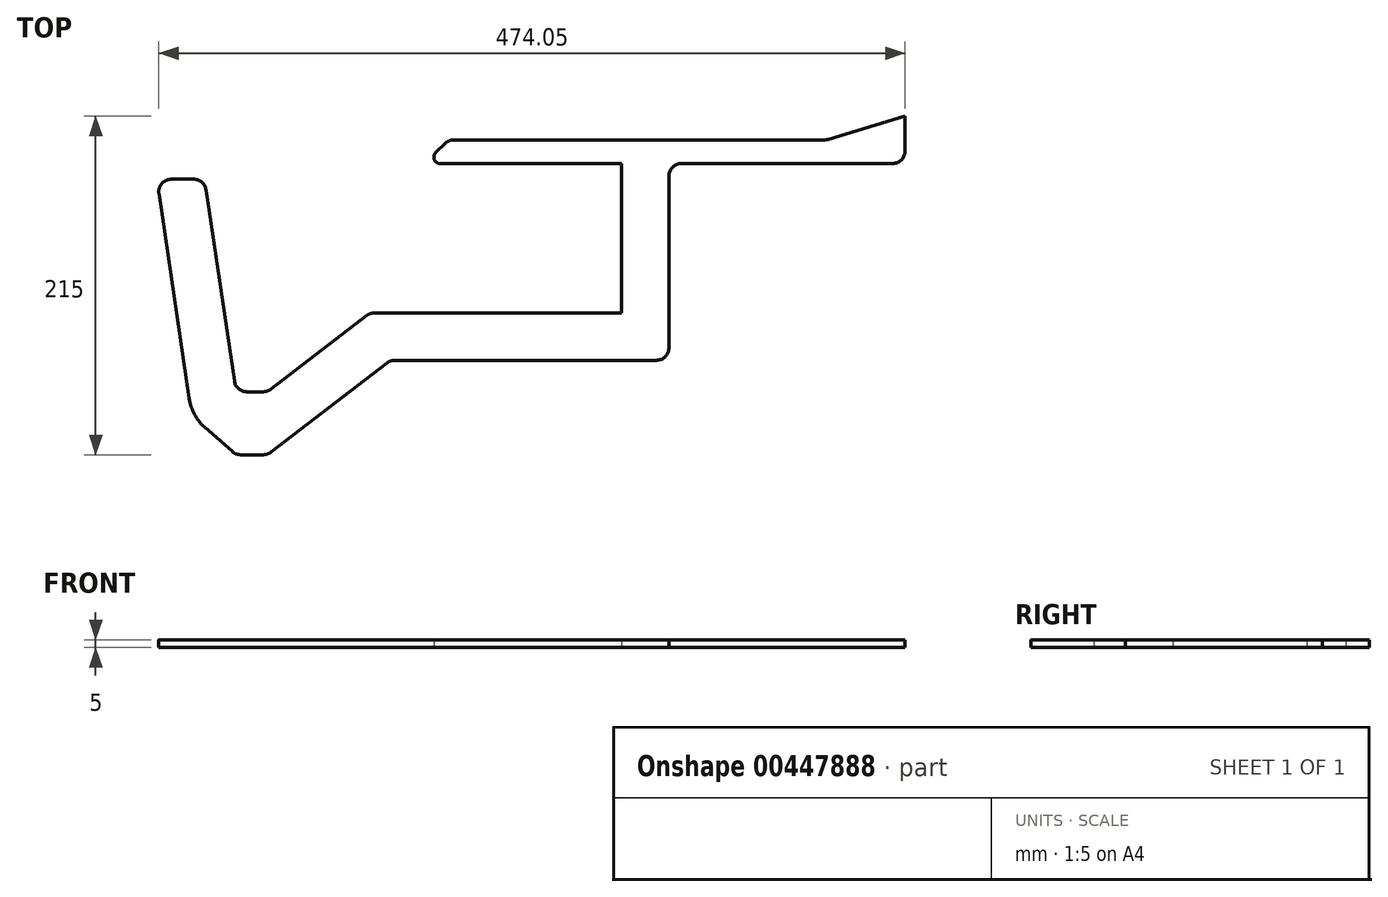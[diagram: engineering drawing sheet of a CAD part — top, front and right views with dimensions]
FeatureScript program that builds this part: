
annotation { "Feature Type Name" : "Feature", "Feature Type Description" : "" }
export const myFeature = defineFeature(function(context is Context, id is Id, definition is map)
    precondition{}
    {
        {
            var Q0;
            Q0=qCreatedBy(makeId("Top.planeOp"),FACE);
            var sketch = newSketch(context, id + "F0", { "sketchPlane" : qUnion([Q0])});
            skPoint(sketch, "E0", {"position": v(-85, 0) * mm});
            skPoint(sketch, "E1", {"position": v(-65, -135) * mm});
            skLineSegment(sketch, "E2", {"start": v(-83.99, -6.83) * mm, "end": v(-66.01, -128.17) * mm});
            skPoint(sketch, "E3", {"position": v(-45, -135) * mm});
            skPoint(sketch, "E4", {"position": v(20, -85) * mm});
            skLineSegment(sketch, "E5", {"start": v(-58.1, -135) * mm, "end": v(-47.72, -135) * mm});
            skLineSegment(sketch, "E6", {"start": v(17.84, -86.66) * mm, "end": v(-42.84, -133.34) * mm});
            skPoint(sketch, "E7", {"position": v(180, -85) * mm});
            skLineSegment(sketch, "E8", {"start": v(22.72, -85) * mm, "end": v(180, -85) * mm});
            skPoint(sketch, "E9", {"position": v(180, 10) * mm});
            skPoint(sketch, "E10", {"position": v(55, 10) * mm});
            skLineSegment(sketch, "E11", {"start": v(64.66, 10) * mm, "end": v(180, 10) * mm});
            skLineSegment(sketch, "E12", {"start": v(180, 10) * mm, "end": v(180, -85) * mm});
            skPoint(sketch, "E13", {"position": v(70, 25) * mm});
            skLineSegment(sketch, "E14", {"start": v(61.83, 16.83) * mm, "end": v(67.66, 22.66) * mm});
            skLineSegment(sketch, "E15", {"start": v(360, 18) * mm, "end": v(360, 40) * mm});
            skLineSegment(sketch, "E16", {"start": v(360, 40) * mm, "end": v(311.12, 25.34) * mm});
            skLineSegment(sketch, "E17", {"start": v(308.83, 25) * mm, "end": v(73.31, 25) * mm});
            skLineSegment(sketch, "E18", {"start": v(352, 10) * mm, "end": v(218, 10) * mm});
            skLineSegment(sketch, "E19", {"start": v(210, 2) * mm, "end": v(210, -107) * mm});
            skPoint(sketch, "E20", {"position": v(-45, -175) * mm});
            skPoint(sketch, "E21", {"position": v(-65, -175) * mm});
            skLineSegment(sketch, "E22", {"start": v(202, -115) * mm, "end": v(35.72, -115) * mm});
            skLineSegment(sketch, "E23", {"start": v(30.84, -116.66) * mm, "end": v(-42.84, -173.34) * mm});
            skLineSegment(sketch, "E24", {"start": v(-61.98, -175) * mm, "end": v(-47.72, -175) * mm});
            skLineSegment(sketch, "E25", {"start": v(-65, -135) * mm, "end": v(-94.68, -139.4) * mm});
            skLineSegment(sketch, "E26", {"start": v(-67.27, -173) * mm, "end": v(-84.84, -157.5) * mm});
            skArc(sketch, "E27", {"start": v(-94.68, -139.4) * mm, "mid": v(-91.36, -149.32) * mm, "end": v(-84.84, -157.5) * mm});
            skLineSegment(sketch, "E28", {"start": v(-94.68, -139.4) * mm, "end": v(-113.97, -9.17) * mm});
            skLineSegment(sketch, "E29", {"start": v(-106.05, 0) * mm, "end": v(-91.9, 0) * mm});
            skPoint(sketch, "E30.visualSharp", {"position": v(-115.33, 0) * mm});
            skArc(sketch, "E30.filletArc", {"start": v(-106.05, 0) * mm, "mid": v(-112.11, -2.77) * mm, "end": v(-113.97, -9.17) * mm});
            skArc(sketch, "E31.filletArc", {"start": v(-67.27, -173) * mm, "mid": v(-64.8, -174.48) * mm, "end": v(-61.98, -175) * mm});
            skArc(sketch, "E32.filletArc", {"start": v(-47.72, -175) * mm, "mid": v(-45.14, -174.57) * mm, "end": v(-42.84, -173.34) * mm});
            skPoint(sketch, "E33.visualSharp", {"position": v(33, -115) * mm});
            skArc(sketch, "E33.filletArc", {"start": v(35.72, -115) * mm, "mid": v(33.14, -115.43) * mm, "end": v(30.84, -116.66) * mm});
            skPoint(sketch, "E34.visualSharp", {"position": v(210, -115) * mm});
            skArc(sketch, "E34.filletArc", {"start": v(202, -115) * mm, "mid": v(207.66, -112.66) * mm, "end": v(210, -107) * mm});
            skPoint(sketch, "E35.visualSharp", {"position": v(210, 10) * mm});
            skArc(sketch, "E35.filletArc", {"start": v(218, 10) * mm, "mid": v(212.34, 7.66) * mm, "end": v(210, 2) * mm});
            skPoint(sketch, "E36.visualSharp", {"position": v(360, 10) * mm});
            skArc(sketch, "E36.filletArc", {"start": v(352, 10) * mm, "mid": v(357.66, 12.34) * mm, "end": v(360, 18) * mm});
            skPoint(sketch, "E37.visualSharp", {"position": v(310, 25) * mm});
            skArc(sketch, "E37.filletArc", {"start": v(308.83, 25) * mm, "mid": v(309.99, 25.08) * mm, "end": v(311.12, 25.34) * mm});
            skArc(sketch, "E38.filletArc", {"start": v(73.31, 25) * mm, "mid": v(70.25, 24.4) * mm, "end": v(67.66, 22.66) * mm});
            skArc(sketch, "E39.filletArc", {"start": v(61.83, 16.83) * mm, "mid": v(60.96, 12.47) * mm, "end": v(64.66, 10) * mm});
            skArc(sketch, "E40.filletArc", {"start": v(-83.99, -6.83) * mm, "mid": v(-86.68, -1.94) * mm, "end": v(-91.9, 0) * mm});
            skArc(sketch, "E41.filletArc", {"start": v(-66.01, -128.17) * mm, "mid": v(-63.32, -133.06) * mm, "end": v(-58.1, -135) * mm});
            skArc(sketch, "E42.filletArc", {"start": v(-47.72, -135) * mm, "mid": v(-45.14, -134.57) * mm, "end": v(-42.84, -133.34) * mm});
            skArc(sketch, "E43.filletArc", {"start": v(22.72, -85) * mm, "mid": v(20.14, -85.43) * mm, "end": v(17.84, -86.66) * mm});
            skPoint(sketch, "E44", {"position": v(0, 0) * mm});
            skSolve(sketch);
        }
        {
            var Q0;
            Q0 = qSketchRegion(id + "F0", true);
            extrude(context, id + "F1", {"entities" : qUnion([Q0]), "depth" : 5 * mm});
        }
    });
